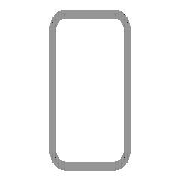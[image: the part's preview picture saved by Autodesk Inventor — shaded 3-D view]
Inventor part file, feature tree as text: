
AUTODESK INVENTOR PART (.ipt)
format: ipt  version: 2024.2 (Build 282272000, 272)  size: 126,464 bytes
history: native  units: mm (DEFAULTED — no unit token found)
features: other x4, sketch x1, plane x1
ambient origin geometry x8: Origin, YZ Plane, XZ Plane, XY Plane, X Axis, Y Axis, Z Axis, Center Point
bodies: Solid1 (feature_tree), Body (feature_tree)
feature tree (6):
  parser-record x1  (decoder bookkeeping rows leaked as tree rows — omitted from the tree; the rows remain in map.json)
  other  "Driven Length"
  other  "Start Plane"
  other  "End Plane"
  sketch  "Sketch3"  dims[d3=2000.0mm d4=0.0mm d7=6.0mm d9=40.0mm d11=80.0mm d12=3.0mm d13=-0.0mm d14=2000.0mm d15=20.0mm d16=40.0mm d17=90.0deg d18=2000.0mm]
  plane  "Work Plane3"
